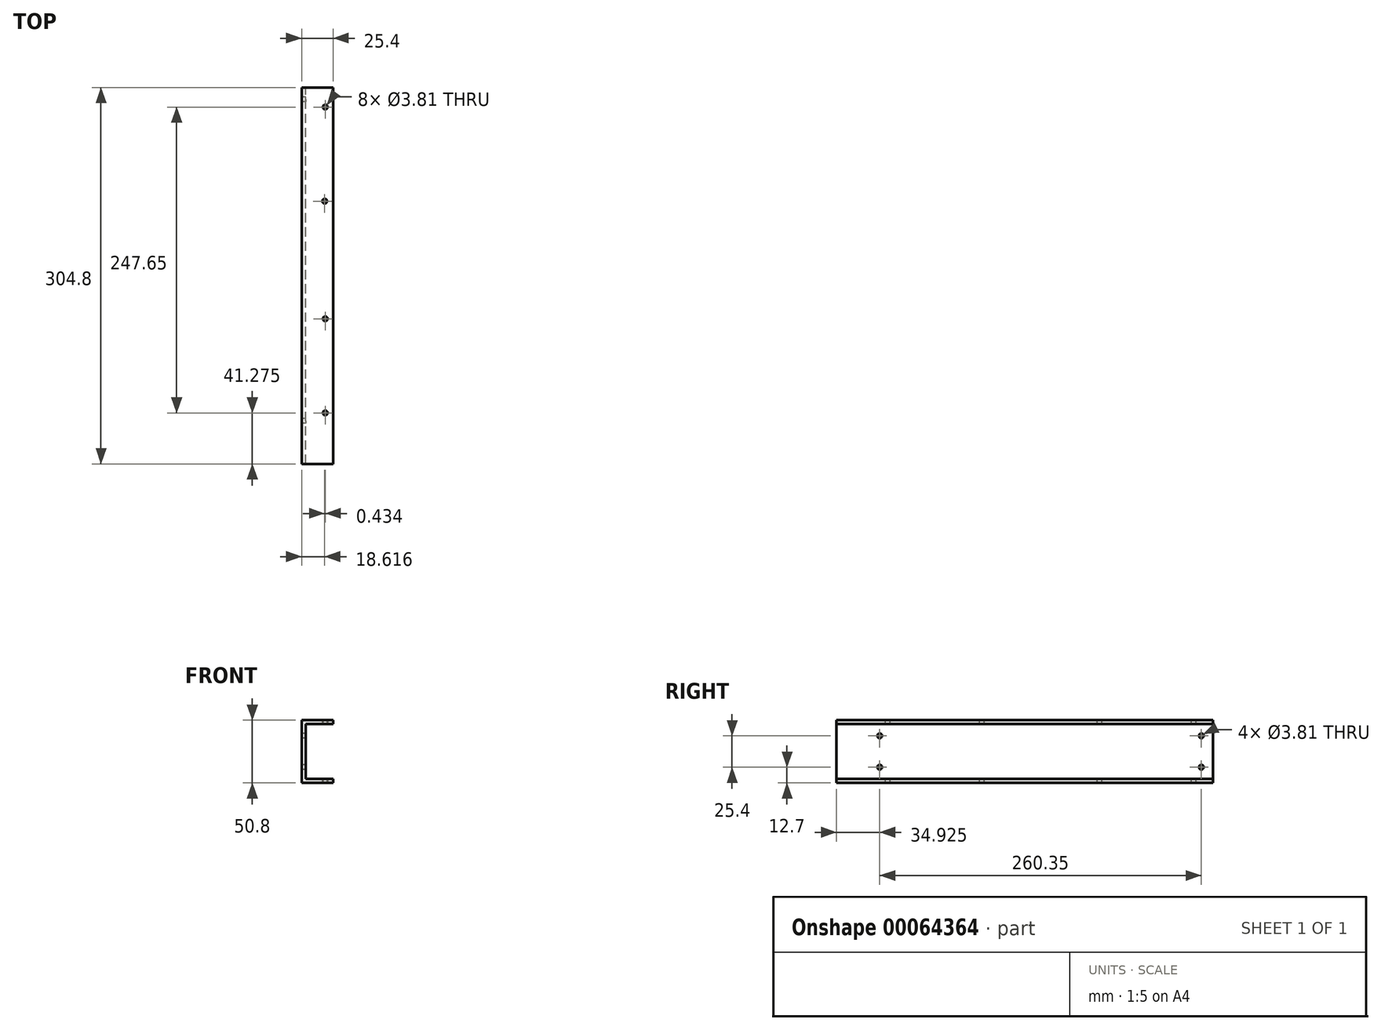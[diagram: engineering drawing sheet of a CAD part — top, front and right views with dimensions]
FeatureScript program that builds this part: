
annotation { "Feature Type Name" : "Feature", "Feature Type Description" : "" }
export const myFeature = defineFeature(function(context is Context, id is Id, definition is map)
    precondition{}
    {
        {
            var Q0;
            Q0=qCreatedBy(makeId("Front.planeOp"),FACE);
            var sketch = newSketch(context, id + "F0", { "sketchPlane" : qUnion([Q0])});
            skLineSegment(sketch, "E0.rect.bottom", {"start": v(-12.7, 25.4) * mm, "end": v(12.7, 25.4) * mm});
            skLineSegment(sketch, "E0.rect.top", {"start": v(-12.7, -25.4) * mm, "end": v(12.7, -25.4) * mm});
            skLineSegment(sketch, "E0.rect.left", {"start": v(-12.7, 25.4) * mm, "end": v(-12.7, -25.4) * mm});
            skLineSegment(sketch, "E0.rect.right", {"start": v(12.7, 25.4) * mm, "end": v(12.7, 22.22) * mm});
            skPoint(sketch, "E0.rect.middle", {"position": v(0, 0) * mm});
            skLineSegment(sketch, "E1.rect.bottom", {"start": v(-9.53, 22.22) * mm, "end": v(12.7, 22.22) * mm});
            skLineSegment(sketch, "E1.rect.top", {"start": v(-9.53, -22.23) * mm, "end": v(12.7, -22.23) * mm});
            skLineSegment(sketch, "E1.rect.left", {"start": v(-9.53, 22.23) * mm, "end": v(-9.53, -22.23) * mm});
            skPoint(sketch, "E2.orphan", {"position": v(9.53, 22.23) * mm});
            skPoint(sketch, "E3.orphan", {"position": v(9.53, -22.23) * mm});
            skLineSegment(sketch, "E4.trimOffspring", {"start": v(12.7, -22.23) * mm, "end": v(12.7, -25.4) * mm});
            skSolve(sketch);
        }
        {
            var Q0;
            Q0=qSketchRegion(id+"F0",true);
            extrude(context, id + "F1", {"entities" : qUnion([Q0]), "endBound" : BoundingType.SYMMETRIC, "depth" : 304.8 * mm});
        }
        {
            var Q0;
            Q0=makeQuery(id+"F1.opExtrude","SWEPT_FACE",FACE,{"disambiguationData":[OSD([sQuery(id+"F0.wireOp",EDGE,"E0.rect.top")])]});
            var sketch = newSketch(context, id + "F2", { "sketchPlane" : qUnion([Q0])});
            skLineSegment(sketch, "E5", {"start": v(6.35, 152.4) * mm, "end": v(6.35, -152.4) * mm});
            skPoint(sketch, "E5.endSnap0", {"position": v(0, -152.4) * mm});
            skPoint(sketch, "E6", {"position": v(6.35, -136.53) * mm});
            skPoint(sketch, "E7", {"position": v(5.92, -60.33) * mm});
            skPoint(sketch, "E8", {"position": v(6.35, 34.92) * mm});
            skPoint(sketch, "E9", {"position": v(6.35, 111.12) * mm});
            skSolve(sketch);
        }
        {
            var Q0;
            Q0=sQuery(id+"F2.wireOp",VERTEX,"E6");
            var Q1;
            Q1=sQuery(id+"F2.wireOp",VERTEX,"E7");
            var Q2;
            Q2=sQuery(id+"F2.wireOp",VERTEX,"E8");
            var Q3;
            Q3=sQuery(id+"F2.wireOp",VERTEX,"E9");
            var Q4;
            Q4=makeQuery(id+"F1.opExtrude","SWEPT_BODY",BODY,{"disambiguationData":[OSD([sQuery(id+"F0.wireOp",EDGE,"E0.rect.bottom"),sQuery(id+"F0.wireOp",EDGE,"E0.rect.top"),sQuery(id+"F0.wireOp",EDGE,"E0.rect.left"),sQuery(id+"F0.wireOp",EDGE,"E0.rect.right"),sQuery(id+"F0.wireOp",EDGE,"E1.rect.bottom"),sQuery(id+"F0.wireOp",EDGE,"E1.rect.top"),sQuery(id+"F0.wireOp",EDGE,"E1.rect.left"),sQuery(id+"F0.wireOp",EDGE,"E4.trimOffspring")])]});
            hole(context, id + "F3", {"style" : HoleStyle.SIMPLE, "holeDiameter" : 3.8 * mm, "endStyle" : HoleEndStyle.THROUGH, "locations" : qUnion([Q0, Q1, Q2, Q3]), "scope" : qUnion([Q4])});
        }
        {
            var Q0;
            Q0=makeQuery(id+"F1.opExtrude","SWEPT_FACE",FACE,{"disambiguationData":[OSD([sQuery(id+"F0.wireOp",EDGE,"E0.rect.left")])]});
            var sketch = newSketch(context, id + "F4", { "sketchPlane" : qUnion([Q0])});
            skPoint(sketch, "E10.positionSnap0", {"position": v(-152.4, 0) * mm});
            skPoint(sketch, "E11.positionSnap0", {"position": v(152.4, 0) * mm});
            skPoint(sketch, "E12", {"position": v(117.47, 12.7) * mm});
            skPoint(sketch, "E13", {"position": v(117.47, -12.7) * mm});
            skPoint(sketch, "E14", {"position": v(-142.88, -12.7) * mm});
            skPoint(sketch, "E15", {"position": v(-142.88, 12.7) * mm});
            skSolve(sketch);
        }
        {
            var Q0;
            Q0=sQuery(id+"F4.wireOp",VERTEX,"E13");
            var Q1;
            Q1=sQuery(id+"F4.wireOp",VERTEX,"E12");
            var Q2;
            Q2=sQuery(id+"F4.wireOp",VERTEX,"E14");
            var Q3;
            Q3=sQuery(id+"F4.wireOp",VERTEX,"E15");
            var Q4;
            Q4=makeQuery(id+"F1.opExtrude","SWEPT_BODY",BODY,{"disambiguationData":[OSD([sQuery(id+"F0.wireOp",EDGE,"E0.rect.bottom"),sQuery(id+"F0.wireOp",EDGE,"E0.rect.top"),sQuery(id+"F0.wireOp",EDGE,"E0.rect.left"),sQuery(id+"F0.wireOp",EDGE,"E0.rect.right"),sQuery(id+"F0.wireOp",EDGE,"E1.rect.bottom"),sQuery(id+"F0.wireOp",EDGE,"E1.rect.top"),sQuery(id+"F0.wireOp",EDGE,"E1.rect.left"),sQuery(id+"F0.wireOp",EDGE,"E4.trimOffspring")])]});
            hole(context, id + "F5", {"style" : HoleStyle.SIMPLE, "holeDiameter" : 3.8 * mm, "endStyle" : HoleEndStyle.THROUGH, "locations" : qUnion([Q0, Q1, Q2, Q3]), "scope" : qUnion([Q4])});
        }
    });
